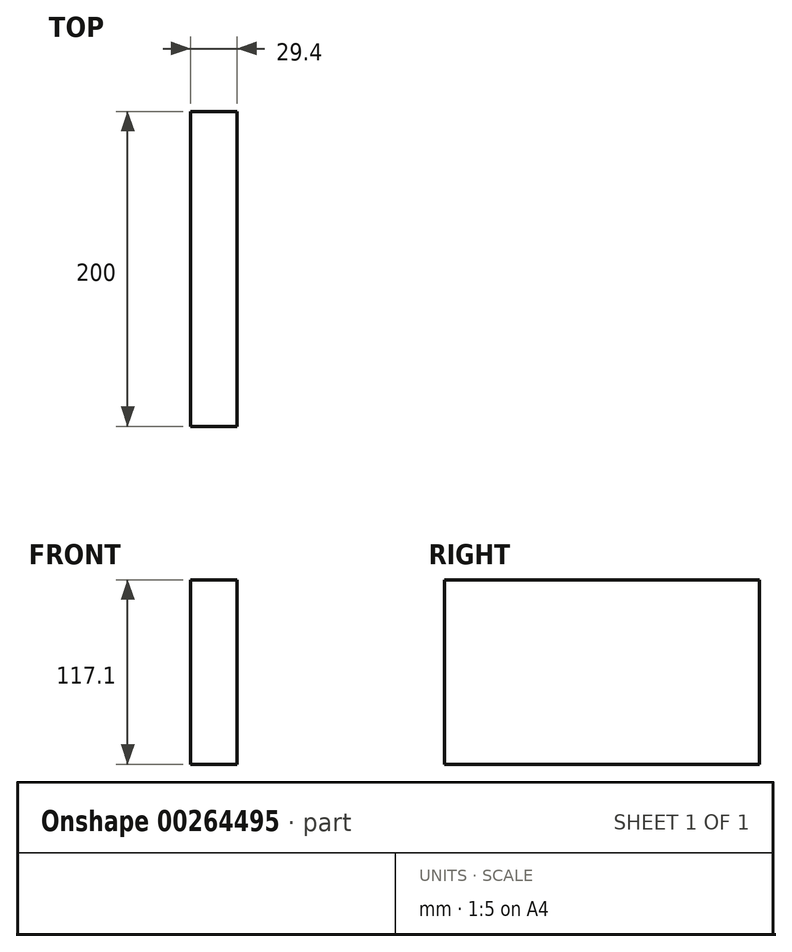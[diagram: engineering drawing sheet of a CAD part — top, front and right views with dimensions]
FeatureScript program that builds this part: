
annotation { "Feature Type Name" : "Feature", "Feature Type Description" : "" }
export const myFeature = defineFeature(function(context is Context, id is Id, definition is map)
    precondition{}
    {
        {
            var Q0;
            Q0=qCreatedBy(makeId("Top.planeOp"),FACE);
            var sketch = newSketch(context, id + "F0", { "sketchPlane" : qUnion([Q0])});
            skLineSegment(sketch, "E0.bottom", {"start": v(-14.7, 100) * mm, "end": v(14.7, 100) * mm});
            skLineSegment(sketch, "E0.top", {"start": v(-14.7, -100) * mm, "end": v(14.7, -100) * mm});
            skLineSegment(sketch, "E0.left", {"start": v(-14.7, 100) * mm, "end": v(-14.7, -100) * mm});
            skLineSegment(sketch, "E0.right", {"start": v(14.7, 100) * mm, "end": v(14.7, -100) * mm});
            skLineSegment(sketch, "E1", {"start": v(0, 0) * mm, "end": v(0, 100) * mm, "construction": true});
            skLineSegment(sketch, "E2", {"start": v(0, 0) * mm, "end": v(14.7, 0) * mm, "construction": true});
            skSolve(sketch);
        }
        {
            var Q0;
            Q0 = qSketchRegion(id + "F0", true);
            extrude(context, id + "F1", {"entities" : qUnion([Q0]), "depth" : 117.1 * mm});
        }
    });
